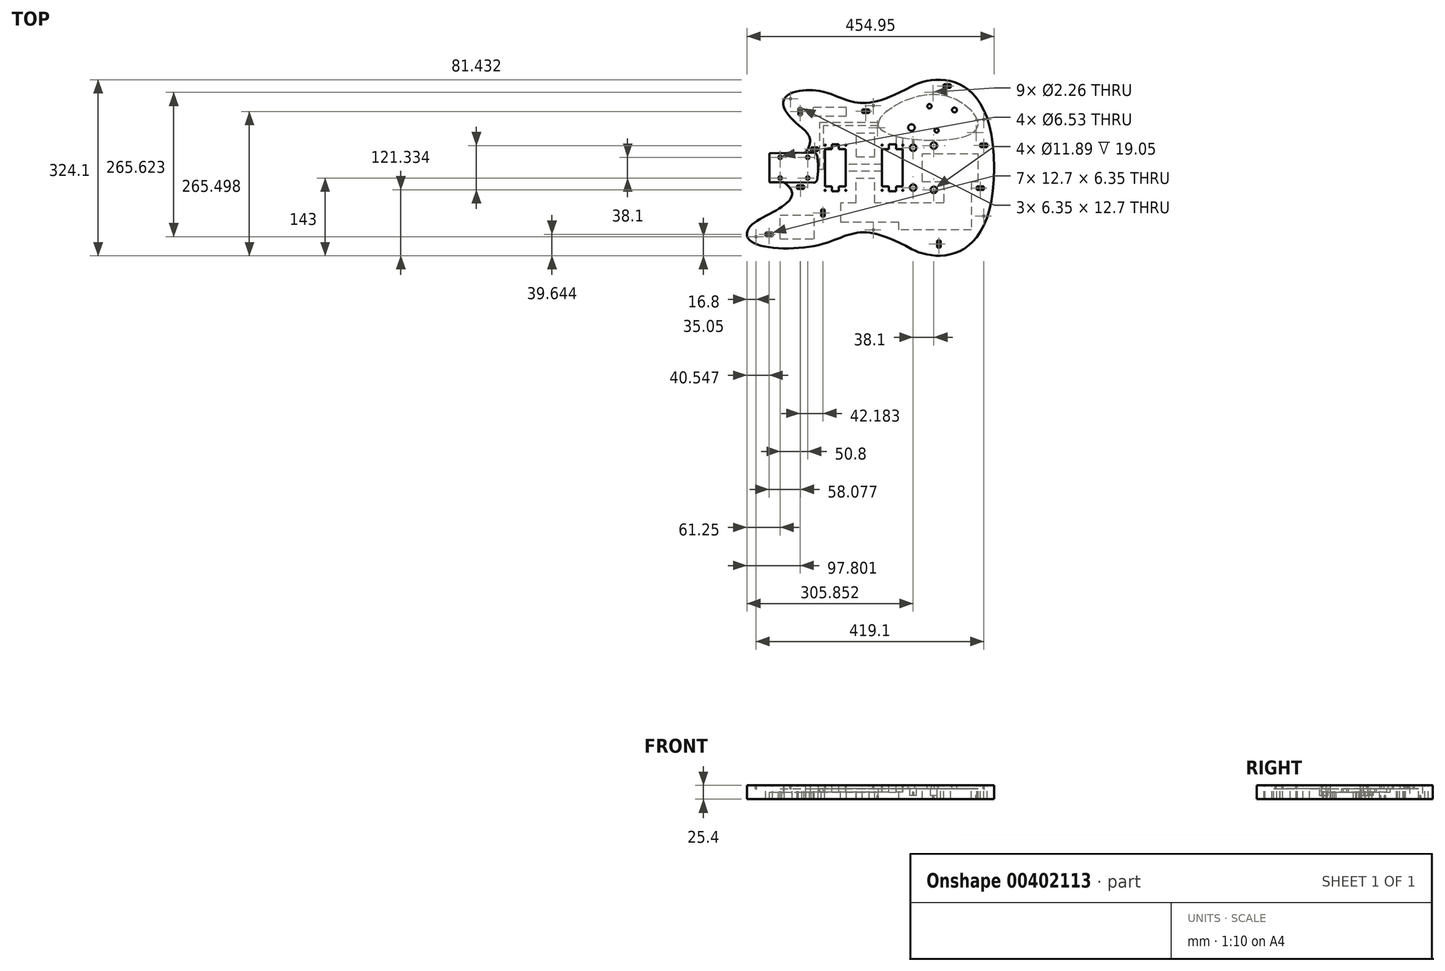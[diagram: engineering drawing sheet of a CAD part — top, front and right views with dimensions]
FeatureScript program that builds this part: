
annotation { "Feature Type Name" : "Feature", "Feature Type Description" : "" }
export const myFeature = defineFeature(function(context is Context, id is Id, definition is map)
    precondition{}
    {
        {
            var Q0;
            Q0=qCreatedBy(makeId("Top.planeOp"),FACE);
            var sketch = newSketch(context, id + "F0", { "sketchPlane" : qUnion([Q0])});
            skLineSegment(sketch, "E0", {"start": v(0, 0) * mm, "end": v(174.75, 0) * mm, "construction": true});
            skLineSegment(sketch, "E1.left", {"start": v(-89.92, 26.64) * mm, "end": v(-89.92, -26.64) * mm});
            skFitSpline(sketch, "E2", {"points": [v(323.85, 0) * mm, v(172.22, 149.85) * mm], "startDerivative": vector(0, 542.74) * mm, "endDerivative": vector(-130.72, -70.42) * mm});
            skFitSpline(sketch, "E3", {"points": [v(172.22, 149.85) * mm, v(16.97, 137.75) * mm], "startDerivative": vector(-268.77, -144.8) * mm, "endDerivative": vector(-154.67, 53.46) * mm});
            skFitSpline(sketch, "E4.MirrorCS", {"points": [v(323.85, 0) * mm, v(172.22, -149.85) * mm], "startDerivative": vector(0, -542.74) * mm, "endDerivative": vector(-130.72, 70.42) * mm});
            skFitSpline(sketch, "E5.MirrorCS", {"points": [v(172.22, -149.85) * mm, v(16.97, -137.75) * mm], "startDerivative": vector(-268.77, 144.8) * mm, "endDerivative": vector(-154.67, -53.46) * mm});
            skFitSpline(sketch, "E6", {"points": [v(16.97, 137.75) * mm, v(-51.36, 136.4) * mm, v(-43.5, 84.96) * mm], "startDerivative": vector(-95.32, 32.95) * mm, "endDerivative": vector(184.33, -175.8) * mm});
            skFitSpline(sketch, "E7", {"points": [v(16.97, -137.75) * mm, v(-127, -110.6) * mm], "startDerivative": vector(-168.94, -58.4) * mm, "endDerivative": vector(81.6, 124.91) * mm});
            skFitSpline(sketch, "E8", {"points": [v(-127, -110.6) * mm, v(-63.65, -26.64) * mm], "startDerivative": vector(46.56, 71.27) * mm, "endDerivative": vector(-162.93, 109.84) * mm});
            skPoint(sketch, "E9", {"position": v(221.8, -162.05) * mm});
            skLineSegment(sketch, "E10", {"start": v(155.1, -162.05) * mm, "end": v(221.8, -162.05) * mm, "construction": true});
            skLineSegment(sketch, "E11", {"start": v(-89.92, 0) * mm, "end": v(0, 0) * mm, "construction": true});
            skLineSegment(sketch, "E12", {"start": v(0, -27.81) * mm, "end": v(0, 27.81) * mm});
            skLineSegment(sketch, "E13", {"start": v(-89.92, -26.64) * mm, "end": v(0, -27.81) * mm});
            skLineSegment(sketch, "E14", {"start": v(-89.92, 26.64) * mm, "end": v(0, 27.81) * mm});
            skArc(sketch, "E15", {"start": v(-3.07, -27.77) * mm, "mid": v(0, 0) * mm, "end": v(-3.07, 27.77) * mm});
            skFitSpline(sketch, "E16", {"points": [v(-43.5, 84.96) * mm, v(-23.84, 27.5) * mm], "startDerivative": vector(45.7, -43.58) * mm, "endDerivative": vector(-71.5, -91.22) * mm});
            skSolve(sketch);
        }
        {
            var Q0;
            Q0=makeQuery(id+"F0.imprint","IMPRINT",FACE,{"disambiguationData":[TD([[makeQuery(id+"F0.imprint","IMPRINT",EDGE,{"derivedFrom":sQuery(id+"F0.wireOp",EDGE,"E2")}),1.0]])]});
            var Q1;
            {var subQ0=sQuery(id+"F0.wireOp",EDGE,"E13");var subQ1=sQuery(id+"F0.wireOp",EDGE,"E12");var subQ2=makeQuery(id+"F0.imprint","INTERSECT",VERTEX,{"derivedFrom":[subQ1,subQ0]});Q1=makeQuery(id+"F0.imprint","IMPRINT",FACE,{"disambiguationData":[TD([[makeQuery(id+"F0.imprint","IMPRINT",EDGE,{"disambiguationData":[TD([[subQ2,-1.0]])],"derivedFrom":subQ1}),1.0]])]});}
            var Q2;
            {var subQ0=sQuery(id+"F0.wireOp",EDGE,"E14");var subQ1=sQuery(id+"F0.wireOp",EDGE,"E12");var subQ2=makeQuery(id+"F0.imprint","INTERSECT",VERTEX,{"derivedFrom":[subQ1,subQ0]});Q2=makeQuery(id+"F0.imprint","IMPRINT",FACE,{"disambiguationData":[TD([[makeQuery(id+"F0.imprint","IMPRINT",EDGE,{"disambiguationData":[TD([[subQ2,1.0]])],"derivedFrom":subQ1}),1.0]])]});}
            extrude(context, id + "F1", {"entities" : qUnion([Q0, Q1, Q2]), "depth" : 12.7 * mm, "hasSecondDirection" : true, "secondDirectionOppositeDirection" : true, "secondDirectionDepth" : 19.05 * mm});
        }
        {
            var Q0;
            {var subQ1=sQuery(id+"F0.wireOp",EDGE,"E1.left");Q0=makeQuery(id+"F0.imprint","IMPRINT",FACE,{"disambiguationData":[TD([[makeQuery(id+"F0.imprint","IMPRINT",EDGE,{"derivedFrom":subQ1}),1.0]])]});}
            extrude(context, id + "F2", {"entities" : qUnion([Q0]), "operationType" : NewBodyOperationType.ADD, "oppositeDirection" : true, "depth" : 19.05 * mm});
        }
        {
            var Q0;
            Q0=makeQuery(id+"F1.opExtrude","CAP_FACE",FACE,{"disambiguationData":[OSD([sQuery(id+"F0.wireOp",EDGE,"E2"),sQuery(id+"F0.wireOp",EDGE,"E3"),sQuery(id+"F0.wireOp",EDGE,"E4.MirrorCS"),sQuery(id+"F0.wireOp",EDGE,"E5.MirrorCS"),sQuery(id+"F0.wireOp",EDGE,"E6"),sQuery(id+"F0.wireOp",EDGE,"9c3daf31-d611-4889-820f-38506a75fe33"),sQuery(id+"F0.wireOp",EDGE,"E7"),sQuery(id+"F0.wireOp",EDGE,"E8"),sQuery(id+"F0.wireOp",EDGE,"E13"),sQuery(id+"F0.wireOp",EDGE,"E14"),sQuery(id+"F0.wireOp",EDGE,"E15")])],"isStart":false});
            var sketch = newSketch(context, id + "F3", { "sketchPlane" : qUnion([Q0])});
            skLineSegment(sketch, "E17", {"start": v(0, 0) * mm, "end": v(174.75, 0) * mm, "construction": true});
            skLineSegment(sketch, "E18", {"start": v(174.75, -36.68) * mm, "end": v(174.75, 36.68) * mm, "construction": true});
            skCircle(sketch, "E19", {"center": v(174.75, -36.68) * mm, "radius": 5.94 * mm});
            skCircle(sketch, "E20", {"center": v(174.75, 36.68) * mm, "radius": 5.94 * mm});
            skLineSegment(sketch, "E21", {"start": v(212.85, -40.72) * mm, "end": v(212.85, 40.72) * mm, "construction": true});
            skLineSegment(sketch, "E22", {"start": v(174.75, 0) * mm, "end": v(212.85, 0) * mm, "construction": true});
            skCircle(sketch, "E23", {"center": v(212.85, -40.72) * mm, "radius": 5.94 * mm});
            skCircle(sketch, "E24", {"center": v(212.85, 40.72) * mm, "radius": 5.94 * mm});
            skSolve(sketch);
        }
        {
            var Q0;
            Q0=makeQuery(id+"F2.opExtrude","CAP_FACE",FACE,{"disambiguationData":[OSD([sQuery(id+"F0.wireOp",EDGE,"E1.left"),sQuery(id+"F0.wireOp",EDGE,"E12"),sQuery(id+"F0.wireOp",EDGE,"E13"),sQuery(id+"F0.wireOp",EDGE,"E14")])],"isStart":true});
            var sketch = newSketch(context, id + "F4", { "sketchPlane" : qUnion([Q0])});
            skPoint(sketch, "E25", {"position": v(-19.05, -19.05) * mm});
            skPoint(sketch, "E26", {"position": v(-69.85, -19.05) * mm});
            skLineSegment(sketch, "E27", {"start": v(0, 0) * mm, "end": v(-89.67, 0) * mm, "construction": true});
            skPoint(sketch, "E28.MirrorP", {"position": v(-19.05, 19.05) * mm});
            skPoint(sketch, "E29.MirrorP", {"position": v(-69.85, 19.05) * mm});
            skSolve(sketch);
        }
        {
            var Q0;
            Q0=sQuery(id+"F4.wireOp",VERTEX,"E25");
            var Q1;
            Q1=sQuery(id+"F4.wireOp",VERTEX,"E26");
            var Q2;
            Q2=sQuery(id+"F4.wireOp",VERTEX,"E29.MirrorP");
            var Q3;
            Q3=sQuery(id+"F4.wireOp",VERTEX,"E28.MirrorP");
            var Q4;
            Q4=makeQuery(id+"F1.opExtrude","SWEPT_BODY",BODY,{"disambiguationData":[OSD([sQuery(id+"F0.wireOp",EDGE,"E2"),sQuery(id+"F0.wireOp",EDGE,"E3"),sQuery(id+"F0.wireOp",EDGE,"E4.MirrorCS"),sQuery(id+"F0.wireOp",EDGE,"E5.MirrorCS"),sQuery(id+"F0.wireOp",EDGE,"E6"),sQuery(id+"F0.wireOp",EDGE,"E7"),sQuery(id+"F0.wireOp",EDGE,"E8"),sQuery(id+"F0.wireOp",EDGE,"E13"),sQuery(id+"F0.wireOp",EDGE,"E14"),sQuery(id+"F0.wireOp",EDGE,"E15"),sQuery(id+"F0.wireOp",EDGE,"E16")])]});
            hole(context, id + "F5", {"style" : HoleStyle.SIMPLE, "endStyle" : HoleEndStyle.THROUGH, "standardTappedOrClearance" : lookupTablePath({ "standard" : "ANSI", "fit" : "Close", "size" : "1/4", "type" : "Clearance" }), "standardBlindInLast" : lookupTablePath({ "fit" : "Close", "standard" : "ANSI", "size" : "1/4", "type" : "Clearance" }), "holeDiameter" : 6.53 * mm, "startFromSketch" : true, "locations" : qUnion([Q0, Q1, Q2, Q3]), "scope" : qUnion([Q4]), "isTappedThrough" : true});
        }
        {
            var Q0;
            Q0=qSketchRegion(id+"F3",true);
            extrude(context, id + "F6", {"entities" : qUnion([Q0]), "operationType" : NewBodyOperationType.REMOVE, "oppositeDirection" : true, "depth" : 19.05 * mm});
        }
        {
            var Q0;
            Q0=makeQuery(id+"F1.opExtrude","CAP_FACE",FACE,{"disambiguationData":[OSD([sQuery(id+"F0.wireOp",EDGE,"E2"),sQuery(id+"F0.wireOp",EDGE,"E3"),sQuery(id+"F0.wireOp",EDGE,"E4.MirrorCS"),sQuery(id+"F0.wireOp",EDGE,"E5.MirrorCS"),sQuery(id+"F0.wireOp",EDGE,"E6"),sQuery(id+"F0.wireOp",EDGE,"9c3daf31-d611-4889-820f-38506a75fe33"),sQuery(id+"F0.wireOp",EDGE,"E7"),sQuery(id+"F0.wireOp",EDGE,"E8"),sQuery(id+"F0.wireOp",EDGE,"E13"),sQuery(id+"F0.wireOp",EDGE,"E14"),sQuery(id+"F0.wireOp",EDGE,"E15")])],"isStart":false});
            var sketch = newSketch(context, id + "F7", { "sketchPlane" : qUnion([Q0])});
            skLineSegment(sketch, "E30", {"start": v(0, 0) * mm, "end": v(384.93, 0) * mm, "construction": true});
            skLineSegment(sketch, "E31.bottom", {"start": v(50.8, -34.3) * mm, "end": v(12.7, -34.3) * mm});
            skLineSegment(sketch, "E31.top", {"start": v(50.8, 34.3) * mm, "end": v(12.7, 34.3) * mm});
            skLineSegment(sketch, "E31.left", {"start": v(50.8, -34.3) * mm, "end": v(50.8, 34.3) * mm});
            skLineSegment(sketch, "E31.right", {"start": v(12.7, -34.3) * mm, "end": v(12.7, 34.3) * mm});
            skPoint(sketch, "E31.middle", {"position": v(31.75, 0) * mm});
            skLineSegment(sketch, "E32.bottom", {"start": v(155.7, -34.3) * mm, "end": v(117.6, -34.3) * mm});
            skLineSegment(sketch, "E32.top", {"start": v(155.7, 34.3) * mm, "end": v(117.6, 34.3) * mm});
            skLineSegment(sketch, "E32.left", {"start": v(155.7, -34.3) * mm, "end": v(155.7, 34.3) * mm});
            skLineSegment(sketch, "E32.right", {"start": v(117.6, -34.3) * mm, "end": v(117.6, 34.3) * mm});
            skPoint(sketch, "E32.middle", {"position": v(136.65, 0) * mm});
            skLineSegment(sketch, "E33.bottom", {"start": v(25.27, 34.3) * mm, "end": v(38.23, 34.3) * mm});
            skLineSegment(sketch, "E33.top", {"start": v(25.27, 43.18) * mm, "end": v(38.23, 43.18) * mm});
            skLineSegment(sketch, "E33.left", {"start": v(25.27, 34.29) * mm, "end": v(25.27, 43.18) * mm});
            skLineSegment(sketch, "E33.right", {"start": v(38.23, 34.29) * mm, "end": v(38.23, 43.18) * mm});
            skPoint(sketch, "E33.middle", {"position": v(31.75, 38.73) * mm});
            skLineSegment(sketch, "E34.MirrorCS", {"start": v(25.27, -34.29) * mm, "end": v(25.27, -43.18) * mm});
            skLineSegment(sketch, "E35.MirrorCS", {"start": v(38.23, -34.29) * mm, "end": v(38.23, -43.18) * mm});
            skLineSegment(sketch, "E36.MirrorCS", {"start": v(25.27, -43.18) * mm, "end": v(38.23, -43.18) * mm});
            skLineSegment(sketch, "E37.bottom", {"start": v(130.17, 34.3) * mm, "end": v(143.13, 34.3) * mm});
            skLineSegment(sketch, "E37.top", {"start": v(130.17, 43.18) * mm, "end": v(143.13, 43.18) * mm});
            skLineSegment(sketch, "E37.left", {"start": v(130.17, 34.3) * mm, "end": v(130.17, 43.18) * mm});
            skLineSegment(sketch, "E37.right", {"start": v(143.13, 34.3) * mm, "end": v(143.13, 43.18) * mm});
            skPoint(sketch, "E37.middle", {"position": v(136.65, 38.74) * mm});
            skLineSegment(sketch, "E38.bottom", {"start": v(130.17, -34.3) * mm, "end": v(143.13, -34.3) * mm});
            skLineSegment(sketch, "E38.top", {"start": v(130.17, -43.18) * mm, "end": v(143.13, -43.18) * mm});
            skLineSegment(sketch, "E38.left", {"start": v(130.17, -34.3) * mm, "end": v(130.17, -43.18) * mm});
            skLineSegment(sketch, "E38.right", {"start": v(143.13, -34.3) * mm, "end": v(143.13, -43.18) * mm});
            skPoint(sketch, "E38.middle", {"position": v(136.65, -38.74) * mm});
            skSolve(sketch);
        }
        {
            var Q0;
            Q0=qSketchRegion(id+"F7",true);
            extrude(context, id + "F8", {"entities" : qUnion([Q0]), "operationType" : NewBodyOperationType.REMOVE, "oppositeDirection" : true, "depth" : 12.7 * mm});
        }
        {
            var Q0;
            Q0=makeQuery(id+"F8.boolean.opBoolean","COPY",FACE,{"derivedFrom":makeQuery(id+"F8.opExtrude","CAP_FACE",FACE,{"disambiguationData":[OSD([sQuery(id+"F7.wireOp",EDGE,"E32.bottom"),sQuery(id+"F7.wireOp",EDGE,"E32.top"),sQuery(id+"F7.wireOp",EDGE,"E32.left"),sQuery(id+"F7.wireOp",EDGE,"E32.right")])],"isStart":false})});
            var sketch = newSketch(context, id + "F9", { "sketchPlane" : qUnion([Q0])});
            skLineSegment(sketch, "E39.bottom", {"start": v(117.6, -6.35) * mm, "end": v(50.8, -6.35) * mm});
            skLineSegment(sketch, "E39.top", {"start": v(117.6, 6.35) * mm, "end": v(50.8, 6.35) * mm});
            skLineSegment(sketch, "E39.left", {"start": v(117.6, -6.35) * mm, "end": v(117.6, 6.35) * mm});
            skLineSegment(sketch, "E39.right", {"start": v(50.8, -6.35) * mm, "end": v(50.8, 6.35) * mm});
            skLineSegment(sketch, "E40", {"start": v(0, 0) * mm, "end": v(50.8, 0) * mm, "construction": true});
            skSolve(sketch);
        }
        {
            var Q0;
            Q0=qSketchRegion(id+"F9",true);
            extrude(context, id + "F10", {"entities" : qUnion([Q0]), "operationType" : NewBodyOperationType.REMOVE, "depth" : 6.35 * mm});
        }
        {
            var Q0;
            {var subQ0=sQuery(id+"F0.wireOp",EDGE,"E15");var subQ1=sQuery(id+"F0.wireOp",EDGE,"E14");var subQ2=sQuery(id+"F0.wireOp",EDGE,"E13");Q0=makeQuery(id+"F1.boolean.opBoolean","MERGE",FACE,{"derivedFrom":[makeQuery(id+"F2.opExtrude","CAP_FACE",FACE,{"disambiguationData":[OSD([sQuery(id+"F0.wireOp",EDGE,"E1.left"),subQ2,subQ1,subQ0])],"isStart":false}),makeQuery(id+"F1.opExtrude","CAP_FACE",FACE,{"disambiguationData":[OSD([sQuery(id+"F0.wireOp",EDGE,"E2"),sQuery(id+"F0.wireOp",EDGE,"E3"),sQuery(id+"F0.wireOp",EDGE,"E4.MirrorCS"),sQuery(id+"F0.wireOp",EDGE,"E5.MirrorCS"),sQuery(id+"F0.wireOp",EDGE,"E6"),sQuery(id+"F0.wireOp",EDGE,"9c3daf31-d611-4889-820f-38506a75fe33"),sQuery(id+"F0.wireOp",EDGE,"E7"),sQuery(id+"F0.wireOp",EDGE,"E8"),subQ2,subQ1,subQ0])],"isStart":true})]});}
            var sketch = newSketch(context, id + "F11", { "sketchPlane" : qUnion([Q0])});
            skFitSpline(sketch, "E41", {"points": [v(110.63, -78.67) * mm, v(217.13, -135.35) * mm, v(294.02, -80) * mm, v(235.47, -50.7) * mm, v(110.63, -78.67) * mm]});
            skFitSpline(sketch, "E42.0", {"points": [v(104.62, -76.23) * mm, v(104.33, -77.7) * mm, v(104.16, -79.2) * mm, v(104.1, -81.17) * mm, v(104.3, -83.63) * mm, v(104.94, -86.5) * mm, v(106.24, -90.22) * mm, v(108.6, -94.67) * mm, v(112.42, -99.8) * mm, v(117.1, -104.76) * mm, v(122.55, -109.58) * mm, v(128.72, -114.24) * mm, v(137.8, -120.2) * mm, v(150.53, -127.06) * mm, v(164.63, -132.8) * mm, v(176.42, -136.5) * mm, v(185.43, -138.78) * mm, v(194.54, -140.49) * mm, v(203.68, -141.56) * mm, v(211.25, -141.87) * mm, v(217.25, -141.73) * mm, v(223.18, -141.32) * mm, v(230.4, -140.33) * mm, v(238.75, -138.44) * mm, v(246.72, -135.92) * mm, v(256.82, -131.82) * mm, v(268.34, -125.5) * mm, v(280.12, -116.5) * mm, v(288.01, -108.26) * mm, v(293.03, -101.42) * mm, v(296.11, -96.2) * mm, v(298.45, -90.92) * mm, v(299.71, -86.48) * mm, v(300.26, -82.92) * mm, v(300.42, -80.24) * mm, v(300.3, -77.57) * mm, v(299.76, -74.1) * mm, v(298.38, -69.97) * mm, v(295.71, -65.52) * mm, v(292.22, -61.64) * mm, v(288.06, -58.29) * mm, v(283.3, -55.4) * mm, v(276.21, -52.08) * mm, v(266.04, -48.78) * mm, v(251.86, -45.97) * mm, v(235.88, -44.18) * mm, v(218.3, -43.34) * mm, v(199.83, -43.47) * mm, v(181.17, -44.57) * mm, v(163.03, -46.67) * mm, v(148.93, -49.28) * mm, v(138.58, -51.92) * mm, v(131.37, -54.2) * mm, v(124.77, -56.8) * mm, v(118.85, -59.75) * mm, v(113.66, -63.15) * mm, v(110.02, -66.48) * mm, v(107.61, -69.53) * mm, v(106.1, -72.05) * mm, v(105.16, -74.32) * mm, v(104.62, -76.23) * mm, v(104.33, -77.7) * mm, v(104.16, -79.2) * mm, v(104.62, -76.23) * mm]});
            skSolve(sketch);
        }
        {
            var Q0;
            Q0=makeQuery(id+"F11.imprint","IMPRINT",FACE,{"disambiguationData":[TD([[makeQuery(id+"F11.imprint","IMPRINT",EDGE,{"derivedFrom":sQuery(id+"F11.wireOp",EDGE,"E41")}),1.0]])]});
            extrude(context, id + "F12", {"entities" : qUnion([Q0]), "operationType" : NewBodyOperationType.REMOVE, "oppositeDirection" : true, "depth" : 25.4 * mm});
        }
        {
            var Q0;
            Q0=makeQuery(id+"F8.boolean.opBoolean","COPY",FACE,{"derivedFrom":makeQuery(id+"F8.opExtrude","SWEPT_FACE",FACE,{"disambiguationData":[OSD([sQuery(id+"F7.wireOp",EDGE,"E32.top")])]})});
            var sketch = newSketch(context, id + "F13", { "sketchPlane" : qUnion([Q0])});
            skLineSegment(sketch, "E43.bottom", {"start": v(143.13, 0) * mm, "end": v(155.7, 0) * mm});
            skLineSegment(sketch, "E43.top", {"start": v(143.13, 6.35) * mm, "end": v(155.7, 6.35) * mm});
            skLineSegment(sketch, "E43.left", {"start": v(143.13, 0) * mm, "end": v(143.13, 6.35) * mm});
            skLineSegment(sketch, "E43.right", {"start": v(155.7, 0) * mm, "end": v(155.7, 6.35) * mm});
            skSolve(sketch);
        }
        {
            var Q0;
            Q0=qSketchRegion(id+"F13",true);
            extrude(context, id + "F14", {"entities" : qUnion([Q0]), "operationType" : NewBodyOperationType.REMOVE, "endBound" : BoundingType.UP_TO_NEXT, "oppositeDirection" : true, "depth" : 25.4 * mm});
        }
        {
            var Q0;
            Q0=makeQuery(id+"F11.imprint","IMPRINT",FACE,{"disambiguationData":[TD([[makeQuery(id+"F11.imprint","IMPRINT",EDGE,{"derivedFrom":sQuery(id+"F11.wireOp",EDGE,"E41")}),-1.0]])]});
            extrude(context, id + "F15", {"entities" : qUnion([Q0]), "operationType" : NewBodyOperationType.REMOVE, "oppositeDirection" : true, "depth" : 6.35 * mm});
        }
        {
            var Q0;
            Q0=makeQuery(id+"F1.opExtrude","SWEPT_EDGE",EDGE,{"disambiguationData":[OSD([sQuery(id+"F0.wireOp",EDGE,"E13"),sQuery(id+"F0.wireOp",EDGE,"E15")])]});
            var Q1;
            Q1=makeQuery(id+"F1.opExtrude","SWEPT_EDGE",EDGE,{"disambiguationData":[OSD([sQuery(id+"F0.wireOp",EDGE,"E14"),sQuery(id+"F0.wireOp",EDGE,"E15")])]});
            fillet(context, id + "F16", {"entities" : qUnion([Q0, Q1]), "radius" : 6.35 * mm, "tangentPropagation" : true, "allowEdgeOverflow" : false});
        }
        {
            var Q0;
            Q0=makeQuery(id+"F1.opExtrude","CAP_FACE",FACE,{"disambiguationData":[OSD([sQuery(id+"F0.wireOp",EDGE,"E2"),sQuery(id+"F0.wireOp",EDGE,"E3"),sQuery(id+"F0.wireOp",EDGE,"E4.MirrorCS"),sQuery(id+"F0.wireOp",EDGE,"E5.MirrorCS"),sQuery(id+"F0.wireOp",EDGE,"E6"),sQuery(id+"F0.wireOp",EDGE,"E7"),sQuery(id+"F0.wireOp",EDGE,"E8"),sQuery(id+"F0.wireOp",EDGE,"E13"),sQuery(id+"F0.wireOp",EDGE,"E14"),sQuery(id+"F0.wireOp",EDGE,"E15"),sQuery(id+"F0.wireOp",EDGE,"E16")])],"isStart":false});
            var sketch = newSketch(context, id + "F17", { "sketchPlane" : qUnion([Q0])});
            skLineSegment(sketch, "E44", {"start": v(0, 0) * mm, "end": v(209, 0) * mm, "construction": true});
            skPoint(sketch, "E44.endSnap0", {"position": v(155.7, 0) * mm});
            skLineSegment(sketch, "E45", {"start": v(110.08, -167.08) * mm, "end": v(428.64, 100.22) * mm});
            skLineSegment(sketch, "E46", {"start": v(428.64, 100.22) * mm, "end": v(469.24, 51.83) * mm});
            skLineSegment(sketch, "E47", {"start": v(469.24, 51.83) * mm, "end": v(150.68, -215.47) * mm});
            skLineSegment(sketch, "E48", {"start": v(150.68, -215.47) * mm, "end": v(110.08, -167.08) * mm});
            skLineSegment(sketch, "E49", {"start": v(469.24, 51.83) * mm, "end": v(485.78, 32.12) * mm});
            skLineSegment(sketch, "E50", {"start": v(485.78, 32.12) * mm, "end": v(167.22, -235.19) * mm});
            skLineSegment(sketch, "E51", {"start": v(167.22, -235.19) * mm, "end": v(150.68, -215.47) * mm});
            skLineSegment(sketch, "E52", {"start": v(277.94, -142.28) * mm, "end": v(220.8, -74.18) * mm, "construction": true});
            skPoint(sketch, "E53", {"position": v(277.94, -142.28) * mm});
            skSolve(sketch);
        }
        {
            var Q0;
            Q0=makeQuery(id+"F11.imprint","IMPRINT",FACE,{"disambiguationData":[TD([[makeQuery(id+"F11.imprint","IMPRINT",EDGE,{"derivedFrom":sQuery(id+"F11.wireOp",EDGE,"E42.0")}),-1.0]])]});
            var sketch = newSketch(context, id + "F18", { "sketchPlane" : qUnion([Q0])});
            skArc(sketch, "E54", {"start": v(-28.79, 147.16) * mm, "mid": v(98.09, 77) * mm, "end": v(215.63, 161.87) * mm});
            skArc(sketch, "E55.0", {"start": v(0, 148.89) * mm, "mid": v(96.56, 102.36) * mm, "end": v(186.84, 160.13) * mm});
            skLineSegment(sketch, "E56", {"start": v(215.63, 161.87) * mm, "end": v(-28.79, 147.16) * mm});
            skFitSpline(sketch, "E57.0", {"points": [v(323.85, 0) * mm, v(323.85, 180.78) * mm, v(215.53, 173.34) * mm, v(172.22, 149.85) * mm]});
            skFitSpline(sketch, "E57.1", {"points": [v(172.22, 149.85) * mm, v(88.93, 104.66) * mm, v(68.52, 119.93) * mm, v(16.97, 137.75) * mm]});
            skFitSpline(sketch, "E57.2", {"points": [v(16.97, 137.75) * mm, v(-39.35, 157.21) * mm, v(-154.2, 152.23) * mm, v(-127, 110.6) * mm]});
            skSolve(sketch);
        }
        {
            var Q0;
            Q0=sQuery(id+"F17.wireOp",EDGE,"E52");
            cPlane(context, id + "F19", {"entities" : qUnion([Q0]), "cplaneType" : CPlaneType.LINE_ANGLE, "offset" : 25.4 * mm, "angle" : 90 * degree, "width" : 152.4 * mm, "height" : 152.4 * mm});
        }
        {
            var Q0;
            Q0=makeQuery(id+"F1.opExtrude","CAP_FACE",FACE,{"disambiguationData":[OSD([sQuery(id+"F0.wireOp",EDGE,"E2"),sQuery(id+"F0.wireOp",EDGE,"E3"),sQuery(id+"F0.wireOp",EDGE,"E4.MirrorCS"),sQuery(id+"F0.wireOp",EDGE,"E5.MirrorCS"),sQuery(id+"F0.wireOp",EDGE,"E6"),sQuery(id+"F0.wireOp",EDGE,"E7"),sQuery(id+"F0.wireOp",EDGE,"E8"),sQuery(id+"F0.wireOp",EDGE,"E13"),sQuery(id+"F0.wireOp",EDGE,"E14"),sQuery(id+"F0.wireOp",EDGE,"E15"),sQuery(id+"F0.wireOp",EDGE,"E16")])],"isStart":false});
            var sketch = newSketch(context, id + "F20", { "sketchPlane" : qUnion([Q0])});
            skCircle(sketch, "E58", {"center": v(171.73, 73.77) * mm, "radius": 6.03 * mm});
            skCircle(sketch, "E59", {"center": v(217.99, 68.51) * mm, "radius": 3.81 * mm});
            skCircle(sketch, "E60", {"center": v(204.83, 113.18) * mm, "radius": 3.94 * mm});
            skLineSegment(sketch, "E61", {"start": v(0, 0) * mm, "end": v(136.07, 0) * mm, "construction": true});
            skLineSegment(sketch, "E62", {"start": v(171.73, 73.77) * mm, "end": v(217.99, 68.51) * mm, "construction": true});
            skLineSegment(sketch, "E63", {"start": v(204.83, 113.18) * mm, "end": v(217.99, 68.51) * mm, "construction": true});
            skLineSegment(sketch, "E64", {"start": v(204.83, 113.18) * mm, "end": v(250.87, 106.22) * mm, "construction": true});
            skCircle(sketch, "E65", {"center": v(250.87, 106.22) * mm, "radius": 4.45 * mm});
            skSolve(sketch);
        }
        {
            var Q0;
            Q0=qSketchRegion(id+"F20",true);
            extrude(context, id + "F21", {"entities" : qUnion([Q0]), "operationType" : NewBodyOperationType.REMOVE, "oppositeDirection" : true, "depth" : 6.35 * mm});
        }
        {
            var Q0;
            Q0=makeQuery(id+"F1.opExtrude","CAP_FACE",FACE,{"disambiguationData":[OSD([sQuery(id+"F0.wireOp",EDGE,"E2"),sQuery(id+"F0.wireOp",EDGE,"E3"),sQuery(id+"F0.wireOp",EDGE,"E4.MirrorCS"),sQuery(id+"F0.wireOp",EDGE,"E5.MirrorCS"),sQuery(id+"F0.wireOp",EDGE,"E6"),sQuery(id+"F0.wireOp",EDGE,"E7"),sQuery(id+"F0.wireOp",EDGE,"E8"),sQuery(id+"F0.wireOp",EDGE,"E13"),sQuery(id+"F0.wireOp",EDGE,"E14"),sQuery(id+"F0.wireOp",EDGE,"E15"),sQuery(id+"F0.wireOp",EDGE,"E16")])],"isStart":false});
            var sketch = newSketch(context, id + "F22", { "sketchPlane" : qUnion([Q0])});
            skPoint(sketch, "E66", {"position": v(-114.3, -127) * mm});
            skPoint(sketch, "E67", {"position": v(101.6, -114.3) * mm});
            skPoint(sketch, "E68", {"position": v(304.8, -88.9) * mm});
            skPoint(sketch, "E69", {"position": v(-50.8, 127) * mm});
            skPoint(sketch, "E70", {"position": v(304.8, 88.9) * mm});
            skPoint(sketch, "E71", {"position": v(101.6, 114.3) * mm});
            skPoint(sketch, "E72", {"position": v(0, 0) * mm});
            skSolve(sketch);
        }
        {
            var Q0;
            Q0=sQuery(id+"F22.wireOp",VERTEX,"E66");
            var Q1;
            Q1=sQuery(id+"F22.wireOp",VERTEX,"E67");
            var Q2;
            Q2=sQuery(id+"F22.wireOp",VERTEX,"E68");
            var Q3;
            Q3=sQuery(id+"F22.wireOp",VERTEX,"E70");
            var Q4;
            Q4=sQuery(id+"F22.wireOp",VERTEX,"E71");
            var Q5;
            Q5=sQuery(id+"F22.wireOp",VERTEX,"E69");
            var Q6;
            Q6=makeQuery(id+"F1.opExtrude","SWEPT_BODY",BODY,{"disambiguationData":[OSD([sQuery(id+"F0.wireOp",EDGE,"E2"),sQuery(id+"F0.wireOp",EDGE,"E3"),sQuery(id+"F0.wireOp",EDGE,"E4.MirrorCS"),sQuery(id+"F0.wireOp",EDGE,"E5.MirrorCS"),sQuery(id+"F0.wireOp",EDGE,"E6"),sQuery(id+"F0.wireOp",EDGE,"E7"),sQuery(id+"F0.wireOp",EDGE,"E8"),sQuery(id+"F0.wireOp",EDGE,"E13"),sQuery(id+"F0.wireOp",EDGE,"E14"),sQuery(id+"F0.wireOp",EDGE,"E15"),sQuery(id+"F0.wireOp",EDGE,"E16")])]});
            hole(context, id + "F23", {"style" : HoleStyle.SIMPLE, "endStyle" : HoleEndStyle.BLIND, "standardTappedOrClearance" : lookupTablePath({ "standard" : "ANSI", "engagement" : "75%", "pitch" : "40 tpi", "size" : "#4", "type" : "Tapped" }), "standardBlindInLast" : lookupTablePath({ "standard" : "ANSI", "engagement" : "75%", "pitch" : "40 tpi", "size" : "#4", "type" : "Tapped" }), "holeDiameter" : 2.26 * mm, "holeDepth" : 6.35 * mm, "startFromSketch" : true, "locations" : qUnion([Q0, Q1, Q2, Q3, Q4, Q5]), "scope" : qUnion([Q6]), "majorDiameter" : 2.84 * mm});
        }
        {
            var Q0;
            Q0=makeQuery(id+"F1.opExtrude","CAP_FACE",FACE,{"disambiguationData":[OSD([sQuery(id+"F0.wireOp",EDGE,"E2"),sQuery(id+"F0.wireOp",EDGE,"E3"),sQuery(id+"F0.wireOp",EDGE,"E4.MirrorCS"),sQuery(id+"F0.wireOp",EDGE,"E5.MirrorCS"),sQuery(id+"F0.wireOp",EDGE,"E6"),sQuery(id+"F0.wireOp",EDGE,"E7"),sQuery(id+"F0.wireOp",EDGE,"E8"),sQuery(id+"F0.wireOp",EDGE,"E13"),sQuery(id+"F0.wireOp",EDGE,"E14"),sQuery(id+"F0.wireOp",EDGE,"E15"),sQuery(id+"F0.wireOp",EDGE,"E16")])],"isStart":false});
            var sketch = newSketch(context, id + "F24", { "sketchPlane" : qUnion([Q0])});
            skLineSegment(sketch, "E73", {"start": v(328.2, -175.68) * mm, "end": v(-147.08, -40.03) * mm});
            skLineSegment(sketch, "E74", {"start": v(-147.08, -40.03) * mm, "end": v(-142.27, -23.17) * mm});
            skLineSegment(sketch, "E75", {"start": v(-142.27, -23.17) * mm, "end": v(301.58, -149.85) * mm});
            skLineSegment(sketch, "E76", {"start": v(301.58, -149.85) * mm, "end": v(328.2, -175.68) * mm});
            skLineSegment(sketch, "E77", {"start": v(350.98, 16.04) * mm, "end": v(162.7, -183.12) * mm});
            skLineSegment(sketch, "E78", {"start": v(162.7, -183.12) * mm, "end": v(152.8, -173.76) * mm});
            skLineSegment(sketch, "E79", {"start": v(152.8, -173.76) * mm, "end": v(340.09, 24.33) * mm});
            skLineSegment(sketch, "E80", {"start": v(340.09, 24.33) * mm, "end": v(350.98, 16.04) * mm});
            skLineSegment(sketch, "E81", {"start": v(237.94, -183.12) * mm, "end": v(122.02, 188.8) * mm});
            skLineSegment(sketch, "E82", {"start": v(122.02, 188.8) * mm, "end": v(109.8, 184.98) * mm});
            skLineSegment(sketch, "E83", {"start": v(109.8, 184.98) * mm, "end": v(224.53, -183.12) * mm});
            skLineSegment(sketch, "E84", {"start": v(224.53, -183.12) * mm, "end": v(237.94, -183.12) * mm});
            skLineSegment(sketch, "E85", {"start": v(371.04, 72.26) * mm, "end": v(-65.05, -175.68) * mm});
            skLineSegment(sketch, "E86", {"start": v(-65.05, -175.68) * mm, "end": v(-75.04, -158.11) * mm});
            skLineSegment(sketch, "E87", {"start": v(-75.04, -158.11) * mm, "end": v(364.99, 92.06) * mm});
            skLineSegment(sketch, "E88", {"start": v(364.99, 92.06) * mm, "end": v(371.04, 72.26) * mm});
            skLineSegment(sketch, "E89", {"start": v(34.3, -183.12) * mm, "end": v(197.87, 194.67) * mm});
            skLineSegment(sketch, "E90", {"start": v(197.87, 194.67) * mm, "end": v(177.23, 200.56) * mm});
            skLineSegment(sketch, "E91", {"start": v(177.23, 200.56) * mm, "end": v(6.7, -193.32) * mm});
            skLineSegment(sketch, "E92", {"start": v(6.7, -193.32) * mm, "end": v(34.3, -183.12) * mm});
            skLineSegment(sketch, "E93", {"start": v(335, -106.85) * mm, "end": v(-19.31, 145.44) * mm});
            skLineSegment(sketch, "E94", {"start": v(-19.31, 145.44) * mm, "end": v(-9.1, 159.8) * mm});
            skLineSegment(sketch, "E95", {"start": v(-9.1, 159.8) * mm, "end": v(342.89, -90.83) * mm});
            skLineSegment(sketch, "E96", {"start": v(342.89, -90.83) * mm, "end": v(335, -106.85) * mm});
            skLineSegment(sketch, "E97", {"start": v(373.04, 34.3) * mm, "end": v(68.82, 144.29) * mm});
            skLineSegment(sketch, "E98", {"start": v(68.82, 144.29) * mm, "end": v(71.85, 152.67) * mm});
            skLineSegment(sketch, "E99", {"start": v(71.85, 152.67) * mm, "end": v(373.9, 43.45) * mm});
            skLineSegment(sketch, "E100", {"start": v(373.9, 43.45) * mm, "end": v(373.04, 34.3) * mm});
            skLineSegment(sketch, "E101", {"start": v(109.72, -174.74) * mm, "end": v(25.1, 196.16) * mm});
            skLineSegment(sketch, "E102", {"start": v(25.1, 196.16) * mm, "end": v(17.84, 193.9) * mm});
            skLineSegment(sketch, "E103", {"start": v(17.84, 193.9) * mm, "end": v(102.4, -176.76) * mm});
            skLineSegment(sketch, "E104", {"start": v(102.4, -176.76) * mm, "end": v(109.72, -174.74) * mm});
            skLineSegment(sketch, "E105", {"start": v(-112.9, 44.04) * mm, "end": v(356.32, 106) * mm});
            skLineSegment(sketch, "E106", {"start": v(356.32, 106) * mm, "end": v(353.8, 125.12) * mm});
            skLineSegment(sketch, "E107", {"start": v(353.8, 125.12) * mm, "end": v(-115.89, 63.11) * mm});
            skLineSegment(sketch, "E108", {"start": v(-115.89, 63.11) * mm, "end": v(-112.9, 44.04) * mm});
            skLineSegment(sketch, "E109", {"start": v(-52.17, -196.4) * mm, "end": v(-6.17, 204.74) * mm});
            skLineSegment(sketch, "E110", {"start": v(-6.17, 204.74) * mm, "end": v(-16.14, 205.89) * mm});
            skLineSegment(sketch, "E111", {"start": v(-16.14, 205.89) * mm, "end": v(-62.15, -195.34) * mm});
            skLineSegment(sketch, "E112", {"start": v(-62.15, -195.34) * mm, "end": v(-52.17, -196.4) * mm});
            skSolve(sketch);
        }
        {
            var Q0;
            Q0=makeQuery(id+"FmjCbHHVVU3nNhI_2.boolean.opBoolean","SPLIT",FACE,{"disambiguationData":[TD([makeQuery(id+"F6.boolean.opBoolean","COPY",FACE,{"derivedFrom":makeQuery(id+"F6.opExtrude","SWEPT_FACE",FACE,{"disambiguationData":[OSD([sQuery(id+"F3.wireOp",EDGE,"E23")])]})})])],"derivedFrom":makeQuery(id+"F1.opExtrude","CAP_FACE",FACE,{"disambiguationData":[OSD([sQuery(id+"F0.wireOp",EDGE,"E2"),sQuery(id+"F0.wireOp",EDGE,"E3"),sQuery(id+"F0.wireOp",EDGE,"E4.MirrorCS"),sQuery(id+"F0.wireOp",EDGE,"E5.MirrorCS"),sQuery(id+"F0.wireOp",EDGE,"E6"),sQuery(id+"F0.wireOp",EDGE,"E7"),sQuery(id+"F0.wireOp",EDGE,"E8"),sQuery(id+"F0.wireOp",EDGE,"E13"),sQuery(id+"F0.wireOp",EDGE,"E14"),sQuery(id+"F0.wireOp",EDGE,"E15"),sQuery(id+"F0.wireOp",EDGE,"E16")])],"isStart":false})});
            var sketch = newSketch(context, id + "F25", { "sketchPlane" : qUnion([Q0])});
            skArc(sketch, "E113", {"start": v(251.47, 197.62) * mm, "mid": v(254.13, 11.8) * mm, "end": v(355.39, -144.01) * mm});
            skArc(sketch, "E114", {"start": v(126.18, 240.99) * mm, "mid": v(210.78, 107.43) * mm, "end": v(356.76, 46.7) * mm});
            skArc(sketch, "E115", {"start": v(161.18, -171.4) * mm, "mid": v(95.8, 15.95) * mm, "end": v(-90.96, -51.07) * mm});
            skArc(sketch, "E116", {"start": v(67.9, -127.6) * mm, "mid": v(-39.6, -110.81) * mm, "end": v(-137.94, -157.4) * mm});
            skArc(sketch, "E117.0", {"start": v(56.11, -140.85) * mm, "mid": v(-38.58, -127.86) * mm, "end": v(-125.02, -168.65) * mm});
            skArc(sketch, "E118.0", {"start": v(150.7, 224.67) * mm, "mid": v(233.35, 113.15) * mm, "end": v(363.44, 64.78) * mm});
            skArc(sketch, "E119.0", {"start": v(227.3, 169.6) * mm, "mid": v(239.32, 0.49) * mm, "end": v(328.89, -143.47) * mm});
            skArc(sketch, "E120.0", {"start": v(141.58, -157.55) * mm, "mid": v(101.96, -14.87) * mm, "end": v(-45.6, -27.22) * mm});
            skLineSegment(sketch, "E121", {"start": v(56.11, -140.85) * mm, "end": v(67.9, -127.6) * mm});
            skArc(sketch, "E122", {"start": v(100.67, -137.14) * mm, "mid": v(226.02, -117.1) * mm, "end": v(335.63, -53.06) * mm});
            skArc(sketch, "E123.0", {"start": v(100.12, -157.96) * mm, "mid": v(233.04, -136.7) * mm, "end": v(349.27, -68.8) * mm});
            skArc(sketch, "E124", {"start": v(-81.3, 71.7) * mm, "mid": v(23.75, 77.25) * mm, "end": v(100.92, 148.73) * mm});
            skArc(sketch, "E125.0", {"start": v(-82.23, 88.3) * mm, "mid": v(15.73, 90.7) * mm, "end": v(87.8, 157.1) * mm});
            skSolve(sketch);
        }
        {
            var Q0;
            Q0=makeQuery(id+"F1.opExtrude","CAP_FACE",FACE,{"disambiguationData":[OSD([sQuery(id+"F0.wireOp",EDGE,"E2"),sQuery(id+"F0.wireOp",EDGE,"E3"),sQuery(id+"F0.wireOp",EDGE,"E4.MirrorCS"),sQuery(id+"F0.wireOp",EDGE,"E5.MirrorCS"),sQuery(id+"F0.wireOp",EDGE,"E6"),sQuery(id+"F0.wireOp",EDGE,"E7"),sQuery(id+"F0.wireOp",EDGE,"E8"),sQuery(id+"F0.wireOp",EDGE,"E13"),sQuery(id+"F0.wireOp",EDGE,"E14"),sQuery(id+"F0.wireOp",EDGE,"E15"),sQuery(id+"F0.wireOp",EDGE,"E16")])],"isStart":false});
            var sketch = newSketch(context, id + "F26", { "sketchPlane" : qUnion([Q0])});
            skLineSegment(sketch, "E126.bottom", {"start": v(12.7, 41.63) * mm, "end": v(50.8, 41.63) * mm});
            skLineSegment(sketch, "E126.top", {"start": v(12.7, -41.63) * mm, "end": v(50.8, -41.63) * mm});
            skLineSegment(sketch, "E126.left", {"start": v(12.7, 41.63) * mm, "end": v(12.7, -41.63) * mm});
            skLineSegment(sketch, "E126.right", {"start": v(50.8, 41.63) * mm, "end": v(50.8, -41.63) * mm});
            skPoint(sketch, "E126.middle", {"position": v(31.75, 0) * mm});
            skLineSegment(sketch, "E127.bottom", {"start": v(117.6, 41.63) * mm, "end": v(155.7, 41.63) * mm});
            skLineSegment(sketch, "E127.top", {"start": v(117.6, -41.63) * mm, "end": v(155.7, -41.63) * mm});
            skLineSegment(sketch, "E127.left", {"start": v(117.6, 41.63) * mm, "end": v(117.6, -41.63) * mm});
            skLineSegment(sketch, "E127.right", {"start": v(155.7, 41.63) * mm, "end": v(155.7, -41.63) * mm});
            skPoint(sketch, "E127.middle", {"position": v(136.65, 0) * mm});
            skLineSegment(sketch, "E128.bottom", {"start": v(8.75, 46.1) * mm, "end": v(54.75, 46.1) * mm});
            skLineSegment(sketch, "E128.top", {"start": v(8.75, -46.1) * mm, "end": v(54.75, -46.1) * mm});
            skLineSegment(sketch, "E128.left", {"start": v(8.75, 46.1) * mm, "end": v(8.75, -46.1) * mm});
            skLineSegment(sketch, "E128.right", {"start": v(54.75, 46.1) * mm, "end": v(54.75, -46.1) * mm});
            skLineSegment(sketch, "E129.bottom", {"start": v(113.65, 46.1) * mm, "end": v(159.65, 46.1) * mm});
            skLineSegment(sketch, "E129.top", {"start": v(113.65, -46.1) * mm, "end": v(159.65, -46.1) * mm});
            skLineSegment(sketch, "E129.left", {"start": v(113.65, 46.1) * mm, "end": v(113.65, -46.1) * mm});
            skLineSegment(sketch, "E129.right", {"start": v(159.65, 46.1) * mm, "end": v(159.65, -46.1) * mm});
            skSolve(sketch);
        }
        {
            var Q0;
            Q0=sQuery(id+"F26.wireOp",VERTEX,"E126.bottom.start");
            var Q1;
            Q1=sQuery(id+"F26.wireOp",VERTEX,"E126.right.start");
            var Q2;
            Q2=sQuery(id+"F26.wireOp",VERTEX,"E126.right.end");
            var Q3;
            Q3=sQuery(id+"F26.wireOp",VERTEX,"E126.left.end");
            var Q4;
            Q4=sQuery(id+"F26.wireOp",VERTEX,"E127.left.start");
            var Q5;
            Q5=sQuery(id+"F26.wireOp",VERTEX,"E127.bottom.end");
            var Q6;
            Q6=sQuery(id+"F26.wireOp",VERTEX,"E127.top.end");
            var Q7;
            Q7=sQuery(id+"F26.wireOp",VERTEX,"E127.top.start");
            var Q8;
            Q8=makeQuery(id+"F1.opExtrude","SWEPT_BODY",BODY,{"disambiguationData":[OSD([sQuery(id+"F0.wireOp",EDGE,"E2"),sQuery(id+"F0.wireOp",EDGE,"E3"),sQuery(id+"F0.wireOp",EDGE,"E4.MirrorCS"),sQuery(id+"F0.wireOp",EDGE,"E5.MirrorCS"),sQuery(id+"F0.wireOp",EDGE,"E6"),sQuery(id+"F0.wireOp",EDGE,"E7"),sQuery(id+"F0.wireOp",EDGE,"E8"),sQuery(id+"F0.wireOp",EDGE,"E13"),sQuery(id+"F0.wireOp",EDGE,"E14"),sQuery(id+"F0.wireOp",EDGE,"E15"),sQuery(id+"F0.wireOp",EDGE,"E16")])]});
            hole(context, id + "F27", {"style" : HoleStyle.SIMPLE, "endStyle" : HoleEndStyle.BLIND, "standardTappedOrClearance" : lookupTablePath({ "standard" : "ANSI", "engagement" : "75%", "pitch" : "48 tpi", "size" : "#3", "type" : "Tapped" }), "standardBlindInLast" : lookupTablePath({ "standard" : "ANSI", "engagement" : "75%", "pitch" : "48 tpi", "size" : "#3", "type" : "Tapped" }), "holeDiameter" : 2 * mm, "holeDepth" : 6.35 * mm, "startFromSketch" : true, "locations" : qUnion([Q0, Q1, Q2, Q3, Q4, Q5, Q6, Q7]), "scope" : qUnion([Q8]), "majorDiameter" : 2.5 * mm});
        }
        {
            var Q0;
            Q0=makeQuery(id+"F1.opExtrude","CAP_FACE",FACE,{"disambiguationData":[OSD([sQuery(id+"F0.wireOp",EDGE,"E2"),sQuery(id+"F0.wireOp",EDGE,"E3"),sQuery(id+"F0.wireOp",EDGE,"E4.MirrorCS"),sQuery(id+"F0.wireOp",EDGE,"E5.MirrorCS"),sQuery(id+"F0.wireOp",EDGE,"E6"),sQuery(id+"F0.wireOp",EDGE,"E7"),sQuery(id+"F0.wireOp",EDGE,"E8"),sQuery(id+"F0.wireOp",EDGE,"E13"),sQuery(id+"F0.wireOp",EDGE,"E14"),sQuery(id+"F0.wireOp",EDGE,"E15"),sQuery(id+"F0.wireOp",EDGE,"E16")])],"isStart":false});
            var sketch = newSketch(context, id + "F28", { "sketchPlane" : qUnion([Q0])});
            skLineSegment(sketch, "E130.bottom", {"start": v(305.03, -40.67) * mm, "end": v(292.33, -40.67) * mm});
            skLineSegment(sketch, "E130.top", {"start": v(305.03, -34.32) * mm, "end": v(292.33, -34.32) * mm});
            skLineSegment(sketch, "E130.left", {"start": v(305.03, -40.67) * mm, "end": v(305.03, -34.32) * mm});
            skLineSegment(sketch, "E130.right", {"start": v(292.33, -40.67) * mm, "end": v(292.33, -34.32) * mm});
            skLineSegment(sketch, "E131.bottom", {"start": v(310.8, 38.2) * mm, "end": v(298.1, 38.2) * mm});
            skLineSegment(sketch, "E131.top", {"start": v(310.8, 44.56) * mm, "end": v(298.1, 44.56) * mm});
            skLineSegment(sketch, "E131.left", {"start": v(310.8, 38.2) * mm, "end": v(310.8, 44.56) * mm});
            skLineSegment(sketch, "E131.right", {"start": v(298.1, 38.2) * mm, "end": v(298.1, 44.56) * mm});
            skLineSegment(sketch, "E132.bottom", {"start": v(218.86, -146.77) * mm, "end": v(225.2, -146.77) * mm});
            skLineSegment(sketch, "E132.top", {"start": v(218.86, -134.07) * mm, "end": v(225.2, -134.07) * mm});
            skLineSegment(sketch, "E132.left", {"start": v(218.86, -146.77) * mm, "end": v(218.86, -134.07) * mm});
            skLineSegment(sketch, "E132.right", {"start": v(225.2, -146.77) * mm, "end": v(225.2, -134.07) * mm});
            skLineSegment(sketch, "E133.bottom", {"start": v(-96.9, -125.58) * mm, "end": v(-84.2, -125.58) * mm});
            skLineSegment(sketch, "E133.top", {"start": v(-96.9, -119.23) * mm, "end": v(-84.2, -119.23) * mm});
            skLineSegment(sketch, "E133.left", {"start": v(-96.9, -125.58) * mm, "end": v(-96.9, -119.23) * mm});
            skLineSegment(sketch, "E133.right", {"start": v(-84.2, -125.58) * mm, "end": v(-84.2, -119.23) * mm});
            skLineSegment(sketch, "E134.bottom", {"start": v(5.7, -89.97) * mm, "end": v(12.06, -89.97) * mm});
            skLineSegment(sketch, "E134.top", {"start": v(5.7, -77.27) * mm, "end": v(12.06, -77.27) * mm});
            skLineSegment(sketch, "E134.left", {"start": v(5.7, -89.97) * mm, "end": v(5.7, -77.27) * mm});
            skLineSegment(sketch, "E134.right", {"start": v(12.06, -89.97) * mm, "end": v(12.06, -77.27) * mm});
            skLineSegment(sketch, "E135.bottom", {"start": v(-36.47, 97.1) * mm, "end": v(-30.12, 97.1) * mm});
            skLineSegment(sketch, "E135.top", {"start": v(-36.47, 109.8) * mm, "end": v(-30.12, 109.8) * mm});
            skLineSegment(sketch, "E135.left", {"start": v(-36.47, 97.1) * mm, "end": v(-36.47, 109.8) * mm});
            skLineSegment(sketch, "E135.right", {"start": v(-30.12, 97.1) * mm, "end": v(-30.12, 109.8) * mm});
            skLineSegment(sketch, "E136.bottom", {"start": v(93.73, 100.54) * mm, "end": v(81.03, 100.54) * mm});
            skLineSegment(sketch, "E136.top", {"start": v(93.73, 106.9) * mm, "end": v(81.03, 106.9) * mm});
            skLineSegment(sketch, "E136.left", {"start": v(93.73, 100.54) * mm, "end": v(93.73, 106.9) * mm});
            skLineSegment(sketch, "E136.right", {"start": v(81.03, 100.54) * mm, "end": v(81.03, 106.9) * mm});
            skLineSegment(sketch, "E137.bottom", {"start": v(243.73, 146.91) * mm, "end": v(231.03, 146.91) * mm});
            skLineSegment(sketch, "E137.top", {"start": v(243.73, 153.26) * mm, "end": v(231.03, 153.26) * mm});
            skLineSegment(sketch, "E137.left", {"start": v(243.73, 146.91) * mm, "end": v(243.73, 153.26) * mm});
            skLineSegment(sketch, "E137.right", {"start": v(231.03, 146.91) * mm, "end": v(231.03, 153.26) * mm});
            skLineSegment(sketch, "E138", {"start": v(-1.15, 0) * mm, "end": v(-21.86, 0) * mm, "construction": true});
            skLineSegment(sketch, "E139.bottom", {"start": v(0, 31.01) * mm, "end": v(-12.7, 31.01) * mm});
            skLineSegment(sketch, "E139.top", {"start": v(0, 37.36) * mm, "end": v(-12.7, 37.36) * mm});
            skLineSegment(sketch, "E139.left", {"start": v(0, 31.01) * mm, "end": v(0, 37.36) * mm});
            skLineSegment(sketch, "E139.right", {"start": v(-12.7, 31.01) * mm, "end": v(-12.7, 37.36) * mm});
            skLineSegment(sketch, "E140.bottom", {"start": v(-26.13, -38.62) * mm, "end": v(-38.83, -38.62) * mm});
            skLineSegment(sketch, "E140.top", {"start": v(-26.13, -32.27) * mm, "end": v(-38.83, -32.27) * mm});
            skLineSegment(sketch, "E140.left", {"start": v(-26.13, -38.62) * mm, "end": v(-26.13, -32.27) * mm});
            skLineSegment(sketch, "E140.right", {"start": v(-38.83, -38.62) * mm, "end": v(-38.83, -32.27) * mm});
            skSolve(sketch);
        }
        {
            var Q0;
            Q0=qSketchRegion(id+"F28",true);
            extrude(context, id + "F29", {"entities" : qUnion([Q0]), "operationType" : NewBodyOperationType.REMOVE, "endBound" : BoundingType.THROUGH_ALL, "oppositeDirection" : true, "depth" : 25.4 * mm});
        }
        {
            var Q0;
            Q0=makeQuery(id+"F15.boolean.opBoolean","COPY",FACE,{"derivedFrom":makeQuery(id+"F15.opExtrude","CAP_FACE",FACE,{"disambiguationData":[OSD([sQuery(id+"F11.wireOp",EDGE,"E41"),sQuery(id+"F11.wireOp",EDGE,"E42.0")])],"isStart":false})});
            var sketch = newSketch(context, id + "F30", { "sketchPlane" : qUnion([Q0])});
            skPoint(sketch, "E141", {"position": v(109.02, -73.47) * mm});
            skLineSegment(sketch, "E142", {"start": v(109.02, -73.47) * mm, "end": v(111.86, -74.9) * mm, "construction": true});
            skLineSegment(sketch, "E143", {"start": v(111.86, -74.9) * mm, "end": v(115.94, -66.86) * mm, "construction": true});
            skPoint(sketch, "E144", {"position": v(211.53, -138.62) * mm});
            skLineSegment(sketch, "E145", {"start": v(211.53, -138.62) * mm, "end": v(211.57, -135.45) * mm, "construction": true});
            skLineSegment(sketch, "E146", {"start": v(211.57, -135.45) * mm, "end": v(209.6, -135.43) * mm, "construction": true});
            skPoint(sketch, "E147", {"position": v(290.52, -64.6) * mm});
            skLineSegment(sketch, "E148", {"start": v(290.52, -64.6) * mm, "end": v(288.27, -66.85) * mm, "construction": true});
            skLineSegment(sketch, "E149", {"start": v(288.27, -66.85) * mm, "end": v(297.29, -75.86) * mm, "construction": true});
            skFitSpline(sketch, "E150.0", {"points": [v(104.35, -77.7) * mm, v(104.27, -78.2) * mm, v(104.16, -79.2) * mm, v(104.1, -81.17) * mm, v(104.3, -83.63) * mm, v(104.94, -86.5) * mm, v(106.24, -90.22) * mm, v(108.6, -94.67) * mm, v(112.42, -99.8) * mm, v(117.1, -104.76) * mm, v(122.55, -109.58) * mm, v(128.72, -114.24) * mm, v(137.8, -120.2) * mm, v(150.53, -127.06) * mm, v(164.63, -132.8) * mm, v(176.42, -136.5) * mm, v(185.43, -138.78) * mm, v(194.54, -140.49) * mm, v(203.68, -141.56) * mm, v(211.25, -141.87) * mm, v(217.25, -141.73) * mm, v(223.18, -141.32) * mm, v(230.4, -140.33) * mm, v(238.75, -138.44) * mm, v(246.72, -135.92) * mm, v(256.82, -131.82) * mm, v(268.34, -125.5) * mm, v(280.12, -116.5) * mm, v(288.01, -108.26) * mm, v(293.03, -101.42) * mm, v(296.11, -96.2) * mm, v(298.45, -90.92) * mm, v(299.71, -86.48) * mm, v(300.26, -82.92) * mm, v(300.42, -80.24) * mm, v(300.3, -77.57) * mm, v(299.76, -74.1) * mm, v(298.38, -69.97) * mm, v(295.71, -65.52) * mm, v(292.22, -61.64) * mm, v(288.06, -58.29) * mm, v(283.3, -55.4) * mm, v(276.21, -52.08) * mm, v(266.04, -48.78) * mm, v(251.86, -45.97) * mm, v(235.88, -44.18) * mm, v(218.3, -43.34) * mm, v(199.83, -43.47) * mm, v(181.17, -44.57) * mm, v(163.03, -46.67) * mm, v(148.93, -49.28) * mm, v(138.58, -51.92) * mm, v(131.37, -54.2) * mm, v(124.77, -56.8) * mm, v(118.85, -59.75) * mm, v(113.66, -63.15) * mm, v(110.02, -66.48) * mm, v(107.61, -69.53) * mm, v(106.1, -72.05) * mm, v(105.16, -74.32) * mm, v(104.62, -76.23) * mm, v(104.43, -77.2) * mm, v(104.35, -77.7) * mm]});
            skFitSpline(sketch, "E151.0", {"points": [v(110.63, -78.67) * mm, v(107.13, -101.27) * mm, v(222.45, -169.94) * mm, v(322.07, -73.8) * mm, v(237.96, -40.61) * mm, v(114.22, -55.4) * mm, v(110.63, -78.67) * mm]});
            skSolve(sketch);
        }
        {
            var Q0;
            Q0=sQuery(id+"F30.wireOp",VERTEX,"E141");
            var Q1;
            Q1=sQuery(id+"F30.wireOp",VERTEX,"E144");
            var Q2;
            Q2=sQuery(id+"F30.wireOp",VERTEX,"E147");
            var Q3;
            Q3=makeQuery(id+"F1.opExtrude","SWEPT_BODY",BODY,{"disambiguationData":[OSD([sQuery(id+"F0.wireOp",EDGE,"E2"),sQuery(id+"F0.wireOp",EDGE,"E3"),sQuery(id+"F0.wireOp",EDGE,"E4.MirrorCS"),sQuery(id+"F0.wireOp",EDGE,"E5.MirrorCS"),sQuery(id+"F0.wireOp",EDGE,"E6"),sQuery(id+"F0.wireOp",EDGE,"E7"),sQuery(id+"F0.wireOp",EDGE,"E8"),sQuery(id+"F0.wireOp",EDGE,"E13"),sQuery(id+"F0.wireOp",EDGE,"E14"),sQuery(id+"F0.wireOp",EDGE,"E15"),sQuery(id+"F0.wireOp",EDGE,"E16")])]});
            hole(context, id + "F31", {"style" : HoleStyle.SIMPLE, "endStyle" : HoleEndStyle.BLIND, "standardTappedOrClearance" : lookupTablePath({ "standard" : "ANSI", "engagement" : "75%", "pitch" : "40 tpi", "size" : "#4", "type" : "Tapped" }), "standardBlindInLast" : lookupTablePath({ "standard" : "ANSI", "engagement" : "75%", "pitch" : "40 tpi", "size" : "#4", "type" : "Tapped" }), "holeDiameter" : 2.26 * mm, "holeDepth" : 6.35 * mm, "startFromSketch" : true, "locations" : qUnion([Q0, Q1, Q2]), "scope" : qUnion([Q3]), "majorDiameter" : 2.84 * mm});
        }
        {
            var Q0;
            Q0=qCreatedBy(makeId("Front.planeOp"),FACE);
            var sketch = newSketch(context, id + "F32", { "sketchPlane" : qUnion([Q0])});
            skLineSegment(sketch, "E152.bottom", {"start": v(337.9, 31.13) * mm, "end": v(-148.37, 31.13) * mm});
            skLineSegment(sketch, "E152.top", {"start": v(337.9, -19.05) * mm, "end": v(-148.37, -19.05) * mm});
            skLineSegment(sketch, "E152.left", {"start": v(337.9, 31.13) * mm, "end": v(337.9, -19.05) * mm});
            skLineSegment(sketch, "E152.right", {"start": v(-148.37, 31.13) * mm, "end": v(-148.37, -19.05) * mm});
            skLineSegment(sketch, "E153.bottom", {"start": v(337.9, 12.7) * mm, "end": v(-148.37, 12.7) * mm});
            skLineSegment(sketch, "E153.top", {"start": v(337.9, 6.35) * mm, "end": v(-148.37, 6.35) * mm});
            skLineSegment(sketch, "E153.left", {"start": v(337.9, 12.7) * mm, "end": v(337.9, 6.35) * mm});
            skLineSegment(sketch, "E153.right", {"start": v(-148.37, 12.7) * mm, "end": v(-148.37, 6.35) * mm});
            skLineSegment(sketch, "E154.bottom", {"start": v(-148.37, 6.35) * mm, "end": v(337.9, 6.35) * mm});
            skLineSegment(sketch, "E154.top", {"start": v(-148.37, 0) * mm, "end": v(337.9, 0) * mm});
            skLineSegment(sketch, "E154.left", {"start": v(-148.37, 6.35) * mm, "end": v(-148.37, 0) * mm});
            skLineSegment(sketch, "E154.right", {"start": v(337.9, 6.35) * mm, "end": v(337.9, 0) * mm});
            skLineSegment(sketch, "E155.bottom", {"start": v(337.9, 0) * mm, "end": v(-148.37, 0) * mm});
            skLineSegment(sketch, "E155.top", {"start": v(337.9, -6.35) * mm, "end": v(-148.37, -6.35) * mm});
            skLineSegment(sketch, "E155.left", {"start": v(337.9, 0) * mm, "end": v(337.9, -6.35) * mm});
            skLineSegment(sketch, "E155.right", {"start": v(-148.37, 0) * mm, "end": v(-148.37, -6.35) * mm});
            skLineSegment(sketch, "E156.bottom", {"start": v(-148.37, -6.35) * mm, "end": v(337.9, -6.35) * mm});
            skLineSegment(sketch, "E156.top", {"start": v(-148.37, -12.7) * mm, "end": v(337.9, -12.7) * mm});
            skLineSegment(sketch, "E156.left", {"start": v(-148.37, -6.35) * mm, "end": v(-148.37, -12.7) * mm});
            skLineSegment(sketch, "E156.right", {"start": v(337.9, -6.35) * mm, "end": v(337.9, -12.7) * mm});
            skLineSegment(sketch, "E157", {"start": v(-148.37, 19.05) * mm, "end": v(337.9, 19.05) * mm});
            skSolve(sketch);
        }
        {
            var Q0;
            Q0=qCreatedBy(makeId("Front.planeOp"),FACE);
            cPlane(context, id + "F33", {"entities" : qUnion([Q0]), "cplaneType" : CPlaneType.OFFSET, "offset" : 152.4 * mm, "width" : 152.4 * mm, "height" : 152.4 * mm});
        }
        {
            var Q0;
            Q0=qCreatedBy(id+"F33.planeOp",FACE);
            var sketch = newSketch(context, id + "F34", { "sketchPlane" : qUnion([Q0])});
            skLineSegment(sketch, "E158", {"start": v(96.2, -63.8) * mm, "end": v(96.2, 0) * mm});
            skArc(sketch, "E159", {"start": v(96.2, 0) * mm, "mid": v(-10.43, -16.33) * mm, "end": v(-107.3, -63.8) * mm});
            skLineSegment(sketch, "E160", {"start": v(-107.3, -63.8) * mm, "end": v(96.2, -63.8) * mm});
            skLineSegment(sketch, "E161", {"start": v(96.2, 0) * mm, "end": v(112.74, 0) * mm, "construction": true});
            skSolve(sketch);
        }
        {
            var Q0;
            {var subQ0=sQuery(id+"F7.wireOp",EDGE,"E32.top");Q0=makeQuery(id+"F8.boolean.opBoolean","COPY",FACE,{"derivedFrom":makeQuery(id+"F8.opExtrude","SWEPT_FACE",FACE,{"disambiguationData":[OSD([subQ0]),TDD([makeQuery(id+"F7.imprint","IMPRINT",EDGE,{"disambiguationData":[TD([[makeQuery(id+"F7.imprint","INTERSECT",VERTEX,{"derivedFrom":[subQ0,sQuery(id+"F7.wireOp",EDGE,"E32.left")]}),-1.0]])],"derivedFrom":subQ0})])]})});}
            var sketch = newSketch(context, id + "F35", { "sketchPlane" : qUnion([Q0])});
            skLineSegment(sketch, "E162.bottom", {"start": v(173.42, 0) * mm, "end": v(175.96, 0) * mm});
            skLineSegment(sketch, "E162.top", {"start": v(173.42, -6.35) * mm, "end": v(175.96, -6.35) * mm});
            skLineSegment(sketch, "E162.left", {"start": v(173.42, 0) * mm, "end": v(173.42, -6.35) * mm});
            skLineSegment(sketch, "E162.right", {"start": v(175.96, 0) * mm, "end": v(175.96, -6.35) * mm});
            skSolve(sketch);
        }
        {
            var Q0;
            Q0=qSketchRegion(id+"F35",true);
            extrude(context, id + "F36", {"entities" : qUnion([Q0]), "operationType" : NewBodyOperationType.REMOVE, "oppositeDirection" : true, "depth" : 25.4 * mm});
        }
        {
            var Q0;
            Q0=makeQuery(id+"F14.boolean.opBoolean","MERGE",FACE,{"derivedFrom":[makeQuery(id+"F12.boolean.opBoolean","COPY",FACE,{"derivedFrom":makeQuery(id+"F12.opExtrude","CAP_FACE",FACE,{"disambiguationData":[OSD([sQuery(id+"F11.wireOp",EDGE,"E41")])],"isStart":false})}),makeQuery(id+"F14.opExtrude","SWEPT_FACE",FACE,{"disambiguationData":[OSD([sQuery(id+"F13.wireOp",EDGE,"E43.top")])]})]});
            var sketch = newSketch(context, id + "F37", { "sketchPlane" : qUnion([Q0])});
            skLineSegment(sketch, "E163", {"start": v(110.87, -77.5) * mm, "end": v(9.27, -77.5) * mm});
            skLineSegment(sketch, "E164", {"start": v(9.27, -77.5) * mm, "end": v(9.27, 3.18) * mm});
            skLineSegment(sketch, "E165", {"start": v(2.92, -3.17) * mm, "end": v(2.92, -83.84) * mm});
            skLineSegment(sketch, "E166", {"start": v(2.92, -83.84) * mm, "end": v(110.87, -83.84) * mm});
            skLineSegment(sketch, "E167", {"start": v(0, 0) * mm, "end": v(-25.83, 0) * mm, "construction": true});
            skLineSegment(sketch, "E168", {"start": v(9.27, 3.18) * mm, "end": v(0, 3.18) * mm});
            skLineSegment(sketch, "E169", {"start": v(2.92, -3.17) * mm, "end": v(0, -3.17) * mm});
            skLineSegment(sketch, "E170", {"start": v(110.87, -77.5) * mm, "end": v(110.87, -83.84) * mm});
            skLineSegment(sketch, "E171", {"start": v(-2.54, 3.18) * mm, "end": v(-2.54, -3.17) * mm});
            skLineSegment(sketch, "E172", {"start": v(-2.54, -3.17) * mm, "end": v(0, -3.17) * mm});
            skLineSegment(sketch, "E173", {"start": v(0, 3.18) * mm, "end": v(-2.54, 3.18) * mm});
            skSolve(sketch);
        }
        {
            var Q0;
            Q0=qSketchRegion(id+"F37",true);
            extrude(context, id + "F38", {"entities" : qUnion([Q0]), "operationType" : NewBodyOperationType.REMOVE, "depth" : 6.35 * mm});
        }
        {
            var Q0;
            Q0=makeQuery(id+"F38.boolean.opBoolean","MERGE",FACE,{"derivedFrom":[makeQuery(id+"F14.boolean.opBoolean","MERGE",FACE,{"derivedFrom":[makeQuery(id+"F12.boolean.opBoolean","COPY",FACE,{"derivedFrom":makeQuery(id+"F12.opExtrude","CAP_FACE",FACE,{"disambiguationData":[OSD([sQuery(id+"F11.wireOp",EDGE,"E41")])],"isStart":false})}),makeQuery(id+"F14.opExtrude","SWEPT_FACE",FACE,{"disambiguationData":[OSD([sQuery(id+"F13.wireOp",EDGE,"E43.top")])]})]}),makeQuery(id+"F38.opExtrude","CAP_FACE",FACE,{"disambiguationData":[OSD([sQuery(id+"F37.wireOp",EDGE,"E163"),sQuery(id+"F37.wireOp",EDGE,"E164"),sQuery(id+"F37.wireOp",EDGE,"E165"),sQuery(id+"F37.wireOp",EDGE,"E166"),sQuery(id+"F37.wireOp",EDGE,"E168"),sQuery(id+"F37.wireOp",EDGE,"E169"),sQuery(id+"F37.wireOp",EDGE,"E170"),sQuery(id+"F37.wireOp",EDGE,"E171"),sQuery(id+"F37.wireOp",EDGE,"E172"),sQuery(id+"F37.wireOp",EDGE,"E173")])],"isStart":true})]});
            var sketch = newSketch(context, id + "F39", { "sketchPlane" : qUnion([Q0])});
            skLineSegment(sketch, "E174.bottom", {"start": v(191.69, 25.65) * mm, "end": v(294.33, 25.65) * mm});
            skLineSegment(sketch, "E174.top", {"start": v(191.69, -25.65) * mm, "end": v(294.33, -25.65) * mm});
            skLineSegment(sketch, "E174.left", {"start": v(191.69, 25.65) * mm, "end": v(191.69, -25.65) * mm});
            skLineSegment(sketch, "E174.right", {"start": v(294.33, 25.65) * mm, "end": v(294.33, -25.65) * mm});
            skPoint(sketch, "E174.middle", {"position": v(243, 0) * mm});
            skLineSegment(sketch, "E175.bottom", {"start": v(282.16, 25.65) * mm, "end": v(231.37, 25.65) * mm});
            skLineSegment(sketch, "E175.top", {"start": v(282.16, 114.54) * mm, "end": v(231.37, 114.54) * mm});
            skLineSegment(sketch, "E175.left", {"start": v(282.16, 25.65) * mm, "end": v(282.16, 114.54) * mm});
            skLineSegment(sketch, "E175.right", {"start": v(231.37, 25.65) * mm, "end": v(231.37, 114.54) * mm});
            skLineSegment(sketch, "E176.bottom", {"start": v(231.37, 114.54) * mm, "end": v(148.3, 114.54) * mm});
            skLineSegment(sketch, "E176.top", {"start": v(231.37, 64.8) * mm, "end": v(148.3, 64.8) * mm});
            skLineSegment(sketch, "E176.left", {"start": v(231.37, 114.54) * mm, "end": v(231.37, 64.8) * mm});
            skLineSegment(sketch, "E176.right", {"start": v(148.3, 114.54) * mm, "end": v(148.3, 64.8) * mm});
            skLineSegment(sketch, "E177.bottom", {"start": v(148.3, 64.8) * mm, "end": v(41.42, 64.8) * mm});
            skLineSegment(sketch, "E177.top", {"start": v(148.3, 100.78) * mm, "end": v(41.42, 100.78) * mm});
            skLineSegment(sketch, "E177.left", {"start": v(148.3, 64.8) * mm, "end": v(148.3, 100.78) * mm});
            skLineSegment(sketch, "E177.right", {"start": v(41.42, 64.8) * mm, "end": v(41.42, 100.78) * mm});
            skLineSegment(sketch, "E178.bottom", {"start": v(-70, 130.76) * mm, "end": v(-7.3, 130.76) * mm});
            skLineSegment(sketch, "E178.top", {"start": v(-70, 87.04) * mm, "end": v(-7.3, 87.04) * mm});
            skLineSegment(sketch, "E178.left", {"start": v(-70, 130.76) * mm, "end": v(-70, 87.04) * mm});
            skLineSegment(sketch, "E178.right", {"start": v(-7.3, 130.76) * mm, "end": v(-7.3, 87.04) * mm});
            skLineSegment(sketch, "E179.bottom", {"start": v(69.61, 64.8) * mm, "end": v(103.85, 64.8) * mm});
            skLineSegment(sketch, "E179.top", {"start": v(69.61, 19.08) * mm, "end": v(103.85, 19.08) * mm});
            skLineSegment(sketch, "E179.left", {"start": v(69.61, 64.8) * mm, "end": v(69.61, 19.08) * mm});
            skLineSegment(sketch, "E179.right", {"start": v(103.85, 64.8) * mm, "end": v(103.85, 19.08) * mm});
            skLineSegment(sketch, "E180.bottom", {"start": v(70.66, -19.9) * mm, "end": v(103.85, -19.9) * mm});
            skLineSegment(sketch, "E180.top", {"start": v(70.66, -64.15) * mm, "end": v(103.85, -64.15) * mm});
            skLineSegment(sketch, "E180.left", {"start": v(70.66, -19.9) * mm, "end": v(70.66, -64.15) * mm});
            skLineSegment(sketch, "E180.right", {"start": v(103.85, -19.9) * mm, "end": v(103.85, -64.15) * mm});
            skLineSegment(sketch, "E181.bottom", {"start": v(-8.88, -95.23) * mm, "end": v(52.23, -95.23) * mm});
            skLineSegment(sketch, "E181.top", {"start": v(-8.88, -111.56) * mm, "end": v(52.23, -111.56) * mm});
            skLineSegment(sketch, "E181.left", {"start": v(-8.88, -95.23) * mm, "end": v(-8.88, -111.56) * mm});
            skLineSegment(sketch, "E181.right", {"start": v(52.23, -95.23) * mm, "end": v(52.23, -111.56) * mm});
            skSolve(sketch);
        }
        {
            var Q0;
            Q0=qSketchRegion(id+"F39",true);
            extrude(context, id + "F40", {"entities" : qUnion([Q0]), "operationType" : NewBodyOperationType.REMOVE, "depth" : 19.05 * mm});
        }
    });
